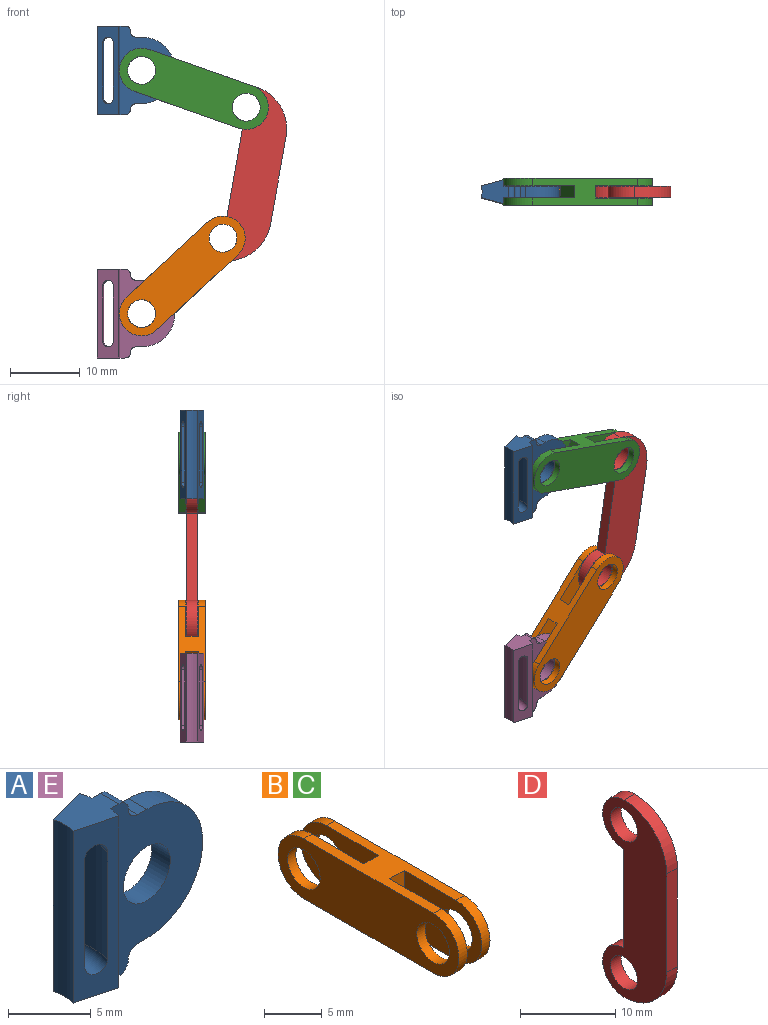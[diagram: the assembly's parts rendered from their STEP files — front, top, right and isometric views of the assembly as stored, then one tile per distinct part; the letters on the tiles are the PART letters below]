
ASSEMBLY  parts=5 mates=8
PART A: 21 faces, bbox 11.1x3.4x12.7 mm
  f0: plane 12.7x3.07mm, normal (-0.26,-0.97,0), area 25.7mm2, adj f1,f2,f3,f4,f17,f18,f19,f20
  f1: cylinder r=6.48mm len=12.7mm, axis (0,0,-1), area 11.4mm2, adj f0,f3,f4,f6
  f2: cylinder r=3.3mm len=12.7mm, axis (0,0,-1), area 22mm2, adj f0,f3,f4,f16
  f3: plane 3.95x3.35mm, normal (0,0,1), area 9.2mm2, adj f0,f1,f2,f5,f6,f7,f12,f16
  f4: plane 3.95x3.35mm, normal (0,0,-1), area 9.2mm2, adj f0,f1,f2,f5,f6,f7,f11,f16
  f5: cylinder r=6.48mm len=12.7mm, axis (0,0,-1), area 11.4mm2, adj f3,f4,f7,f16
  f6: plane 12.7x7.86mm, normal (0,-1,0), area 57.4mm2, adj f1,f3,f4,f8,f9,f10,f11,f12
  f7: plane 12.7x7.86mm, normal (0,1,0), area 57.4mm2, adj f3,f4,f5,f8,f9,f10,f11,f12
  f8: plane 1.59x0.79mm, normal (0,0,-1), area 1.3mm2, adj f6,f7,f10,f14
  f9: plane 1.59x0.79mm, normal (0,0,1), area 1.3mm2, adj f6,f7,f13,f14
  f10: cylinder r=0.79mm len=1.59mm, axis (0,-1,0), area 2mm2, adj f6,f7,f8,f11
  f11: cylinder r=0.79mm len=1.59mm, axis (0,-1,0), area 2mm2, adj f4,f6,f7,f10
  f12: cylinder r=0.79mm len=1.59mm, axis (0,1,0), area 2mm2, adj f3,f6,f7,f13
  f13: cylinder r=0.79mm len=1.59mm, axis (0,-1,0), area 2mm2, adj f6,f7,f9,f12
  f14: cylinder r=4.76mm len=9.53mm, axis (0,1,0), area 23.8mm2, adj f6,f7,f8,f9
  f15: cylinder r=2mm len=4mm, axis (0,-1,0), area 19.9mm2, adj f6,f7
  f16: plane 12.7x3.07mm, normal (-0.26,0.97,0), area 25.7mm2, adj f2,f3,f4,f5,f17,f18,f19,f20
  f17: cylinder r=4.1mm len=7.94mm, axis (0,0,1), area 17mm2, adj f0,f16,f19,f20
  f18: cylinder r=5.68mm len=7.94mm, axis (0,0,1), area 23.6mm2, adj f0,f16,f19,f20
  f19: torus R=4.89mm, axis (0,0,1), area 6.4mm2, adj f0,f16,f17,f18
  f20: torus R=4.89mm, axis (0,0,1), area 6.4mm2, adj f0,f16,f17,f18
PART B: 18 faces, bbox 3.8x22.2x6.4 mm
  f0: plane 6.35x1.78mm, normal (0,-1,0), area 11.3mm2, adj f1,f3,f6,f7
  f1: plane 15.88x3.81mm, normal (0,0,-1), area 37.9mm2, adj f0,f2,f4,f5,f6,f7,f8,f9
  f2: plane 6.35x1.78mm, normal (0,1,0), area 11.3mm2, adj f1,f3,f5,f9
  f3: plane 15.88x3.81mm, normal (0,0,1), area 37.9mm2, adj f0,f2,f4,f5,f6,f7,f8,f9
  f4: plane 22.23x6.35mm, normal (1,0,0), area 107.3mm2, adj f1,f3,f10,f13,f15,f17
  f5: plane 9.53x6.35mm, normal (-1,0,0), area 43.6mm2, adj f1,f2,f3,f10,f17
  f6: plane 9.53x6.35mm, normal (-1,0,0), area 43.6mm2, adj f0,f1,f3,f13,f15
  f7: plane 9.53x6.35mm, normal (1,0,0), area 43.6mm2, adj f0,f1,f3,f12,f14
  f8: plane 22.23x6.35mm, normal (-1,0,0), area 107.3mm2, adj f1,f3,f11,f12,f14,f16
  f9: plane 9.53x6.35mm, normal (1,0,0), area 43.6mm2, adj f1,f2,f3,f11,f16
  f10: cylinder r=3.17mm len=6.35mm, axis (1,0,0), area 10.1mm2, adj f1,f3,f4,f5
  f11: cylinder r=3.17mm len=6.35mm, axis (1,0,0), area 10.1mm2, adj f1,f3,f8,f9
  f12: cylinder r=3.17mm len=6.35mm, axis (-1,0,0), area 10.1mm2, adj f1,f3,f7,f8
  f13: cylinder r=3.17mm len=6.35mm, axis (-1,0,0), area 10.1mm2, adj f1,f3,f4,f6
  f14: cylinder r=2mm len=4mm, axis (1,0,0), area 12.8mm2, adj f7,f8
  f15: cylinder r=2mm len=4mm, axis (1,0,0), area 12.8mm2, adj f4,f6
  f16: cylinder r=2mm len=4mm, axis (1,0,0), area 12.8mm2, adj f8,f9
  f17: cylinder r=2mm len=4mm, axis (1,0,0), area 12.8mm2, adj f4,f5
PART C: same geometry as B
PART D: 10 faces, bbox 1.6x9.5x25.4 mm
  f0: plane 12.7x1.59mm, normal (0,1,0), area 20.2mm2, adj f1,f5,f6,f7
  f1: cylinder r=3.17mm len=6.35mm, axis (-1,0,0), area 15.8mm2, adj f0,f2,f6,f7
  f2: cylinder r=6.35mm len=6.35mm, axis (-1,0,0), area 15.8mm2, adj f1,f3,f6,f7
  f3: plane 12.7x1.59mm, normal (0,-1,0), area 20.2mm2, adj f2,f4,f6,f7
  f4: cylinder r=6.35mm len=6.35mm, axis (-1,0,0), area 15.8mm2, adj f3,f5,f6,f7
  f5: cylinder r=3.17mm len=6.35mm, axis (-1,0,0), area 15.8mm2, adj f0,f4,f6,f7
  f6: plane 25.4x9.53mm, normal (1,0,0), area 150.5mm2, adj f0,f1,f2,f3,f4,f5,f8,f9
  f7: plane 25.4x9.53mm, normal (-1,0,0), area 150.5mm2, adj f0,f1,f2,f3,f4,f5,f8,f9
  f8: cylinder r=2mm len=4mm, axis (1,0,0), area 19.9mm2, adj f6,f7
  f9: cylinder r=2mm len=4mm, axis (1,0,0), area 19.9mm2, adj f6,f7
PART E: same geometry as A
PLACE A t=(-16.74,10.83,33.89)mm fixed
PLACE B rot(axis=(0.68,0.68,0.27),150.1deg) t=(-1.39,10.83,4.46)mm
PLACE C rot(axis=(0.7,-0.7,-0.12),166.3deg) t=(0.27,10.83,31.25)mm
PLACE D rot(axis=(0.09,0.09,0.99),90.4deg) t=(9.22,10.83,18.68)mm
PLACE E rot(axis=(-0.04,-0.11,-0.99),0deg) t=(-16.74,10.83,-0.93)mm
MATE cylindrical D.f1 <-> C.f14  axis (0,1,0) through (7.76,10.83,28.61)mm
MATE cylindrical C.f11 <-> A.f14  axis (0,-1,0) through (-7.21,10.83,33.89)mm
MATE planar C.f11 <-> A.f14  axis (0,-1,0) through (-7.21,10.83,33.89)mm
MATE planar D.f5 <-> B.f11  axis (0,1,0) through (4.44,10.83,9.85)mm
MATE planar C.f14 <-> D.f1  axis (0,1,0) through (7.76,10.83,28.61)mm
MATE cylindrical D.f5 <-> B.f11  axis (0,1,0) through (4.44,10.83,9.85)mm
MATE cylindrical A.f1 <-> E.f1  axis (0,0,-1) through (-16.74,10.83,27.54)mm
MATE cylindrical B.f14 <-> E.f14  axis (0,-1,0) through (-7.21,10.83,-0.93)mm
